# Revit family: xxxTowel_Hook-Whitehall_Mfg-Dignity_Suite-WHD-TH-Series
name_source: partatom
category: Specialty Equipment
units: mm (PartAtom-declared; Revit-internal decimal feet)

## family parameters
Cut with Voids When Loaded = No
Host = Face
OmniClass Number = 23.40.20.21.31
OmniClass Title = Robe Hooks
Part Type = Normal
Room Calculation Point = No
Round Connector Dimension = Use Diameter
Shared = Yes

## types (3) — shared parameters
ADA Compliant = Yes
Assembly Code = C1030220
Compliance Certifications = Member of U.S. Green Building Council, Recyclable Product
Default Elevation = 40"
Installation Type = Wall Mounted
Length = 7/8"
Manufacturer = Whitehall Manufacturing
Max. Load Capacity = 11 lbs.
URL = https://www.whitehallmfg.com
Width = 3 1/8"

## per-type parameters (varying)
| type | Description | Finish | Material |
| WHD-TH-WHITE | Ligature Resistant Towel/Clothes Hook- White | Plastic-Whitehall Mfg-White | Plastic-Whitehall Mfg-White |
| WHD-TH-BLUE | Ligature Resistant Towel/Clothes Hook- Blue | Plastic-Whitehall Mfg-Blue | Plastic-Whitehall Mfg-Blue |
| WHD-TH-GRAY | Ligature Resistant Towel/Clothes Hook- Gray | Plastic-Whitehall Mfg-Gray | Plastic-Whitehall Mfg-Gray |

note: column(s) folded — value = type name in every type: Model

## geometry (parser evidence)
native form markers: Sweep x2
no freeform markers — native parametric forms only
